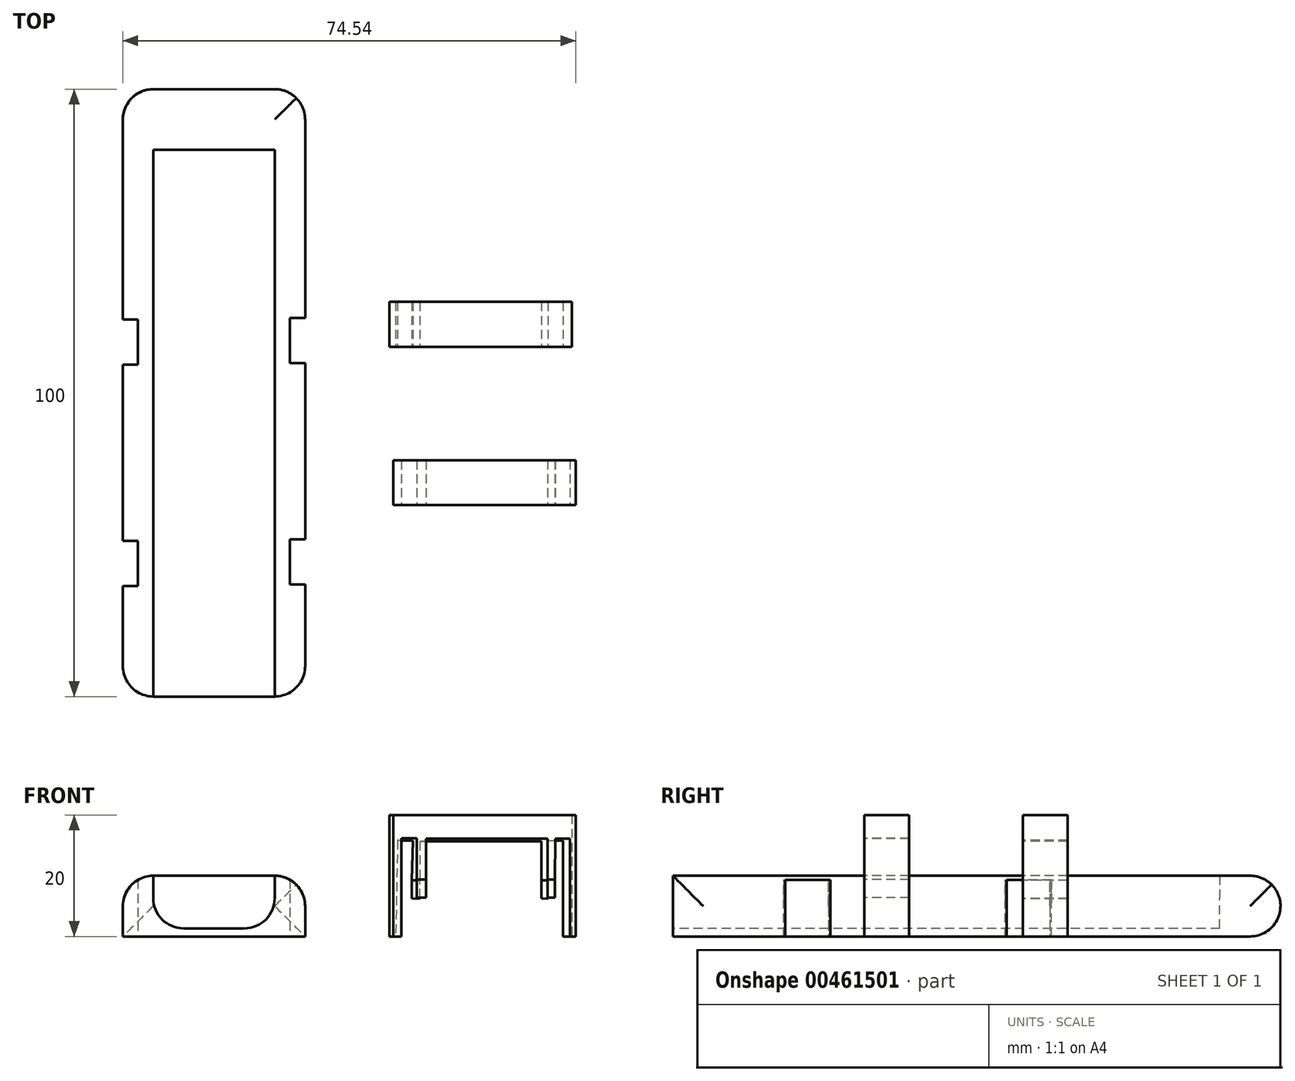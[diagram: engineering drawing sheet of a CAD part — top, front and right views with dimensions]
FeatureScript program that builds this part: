
annotation { "Feature Type Name" : "Feature", "Feature Type Description" : "" }
export const myFeature = defineFeature(function(context is Context, id is Id, definition is map)
    precondition{}
    {
        {
            var Q0;
            Q0=qCreatedBy(makeId("Top.planeOp"),FACE);
            var sketch = newSketch(context, id + "F0", { "sketchPlane" : qUnion([Q0])});
            skLineSegment(sketch, "E0.bottom", {"start": v(-21.76, -47.78) * mm, "end": v(8.24, -47.78) * mm});
            skLineSegment(sketch, "E0.top", {"start": v(-21.76, 52.22) * mm, "end": v(8.24, 52.22) * mm});
            skLineSegment(sketch, "E0.left", {"start": v(-21.76, -47.78) * mm, "end": v(-21.76, 52.22) * mm});
            skLineSegment(sketch, "E0.right", {"start": v(8.24, -47.78) * mm, "end": v(8.24, 52.22) * mm});
            skSolve(sketch);
        }
        {
            var Q0;
            Q0=makeQuery(id+"F0.imprint","IMPRINT",FACE,{"disambiguationData":[TD([[makeQuery(id+"F0.imprint","IMPRINT",EDGE,{"derivedFrom":sQuery(id+"F0.wireOp",EDGE,"E0.bottom")}),1.0]])]});
            extrude(context, id + "F1", {"entities" : qUnion([Q0]), "depth" : 10 * mm});
        }
        {
            var Q0;
            Q0=makeQuery(id+"F1.opExtrude","SWEPT_FACE",FACE,{"disambiguationData":[OSD([sQuery(id+"F0.wireOp",EDGE,"E0.bottom")])]});
            var sketch = newSketch(context, id + "F2", { "sketchPlane" : qUnion([Q0])});
            skLineSegment(sketch, "E1", {"start": v(-21.76, 10) * mm, "end": v(-16.76, 10) * mm});
            skLineSegment(sketch, "E2", {"start": v(-16.76, 10) * mm, "end": v(-16.76, 1.33) * mm});
            skLineSegment(sketch, "E3", {"start": v(-16.76, 1.33) * mm, "end": v(3.24, 1.33) * mm});
            skLineSegment(sketch, "E4", {"start": v(3.24, 1.33) * mm, "end": v(3.24, 10) * mm});
            skLineSegment(sketch, "E5", {"start": v(3.24, 10) * mm, "end": v(8.24, 10) * mm});
            skLineSegment(sketch, "E6", {"start": v(8.24, 10) * mm, "end": v(8.24, 0) * mm});
            skLineSegment(sketch, "E7", {"start": v(8.24, 0) * mm, "end": v(-21.76, 0) * mm});
            skLineSegment(sketch, "E8", {"start": v(-21.76, 0) * mm, "end": v(-21.76, 10) * mm});
            skSolve(sketch);
        }
        {
            var Q0;
            {var subQ0=sQuery(id+"F2.wireOp",EDGE,"E2");Q0=makeQuery(id+"F2.imprint","IMPRINT",FACE,{"disambiguationData":[TD([[makeQuery(id+"F2.imprint","IMPRINT",EDGE,{"derivedFrom":subQ0}),1.0]])]});}
            extrude(context, id + "F3", {"entities" : qUnion([Q0]), "operationType" : NewBodyOperationType.REMOVE, "oppositeDirection" : true, "depth" : 90 * mm});
        }
        {
            var Q0;
            Q0=makeQuery(id+"F3.boolean.opBoolean","COPY",EDGE,{"derivedFrom":makeQuery(id+"F3.opExtrude","CAP_EDGE",EDGE,{"disambiguationData":[OSD([sQuery(id+"F0.wireOp",EDGE,"E0.bottom")])],"isStart":false})});
            var Q1;
            Q1=makeQuery(id+"F1.opExtrude","CAP_EDGE",EDGE,{"disambiguationData":[OSD([sQuery(id+"F0.wireOp",EDGE,"E0.top")])],"isStart":false});
            var Q2;
            Q2=makeQuery(id+"F1.opExtrude","CAP_EDGE",EDGE,{"disambiguationData":[OSD([sQuery(id+"F0.wireOp",EDGE,"E0.top")])],"isStart":true});
            var Q3;
            Q3=makeQuery(id+"F1.opExtrude","SWEPT_EDGE",EDGE,{"disambiguationData":[OSD([sQuery(id+"F0.wireOp",EDGE,"E0.top"),sQuery(id+"F0.wireOp",EDGE,"E0.right")])]});
            var Q4;
            Q4=makeQuery(id+"F1.opExtrude","SWEPT_EDGE",EDGE,{"disambiguationData":[OSD([sQuery(id+"F0.wireOp",EDGE,"E0.top"),sQuery(id+"F0.wireOp",EDGE,"E0.left")])]});
            fillet(context, id + "F4", {"entities" : qUnion([Q0, Q1, Q2, Q3, Q4]), "radius" : 5 * mm, "tangentPropagation" : true, "allowEdgeOverflow" : false});
        }
        {
            var Q0;
            Q0=makeQuery(id+"F1.opExtrude","SWEPT_FACE",FACE,{"disambiguationData":[OSD([sQuery(id+"F0.wireOp",EDGE,"E0.right")])]});
            var sketch = newSketch(context, id + "F5", { "sketchPlane" : qUnion([Q0])});
            skLineSegment(sketch, "E9", {"start": v(-29.31, 10) * mm, "end": v(-29.31, 1.65) * mm});
            skLineSegment(sketch, "E10", {"start": v(-29.31, 1.65) * mm, "end": v(-21.88, 1.65) * mm});
            skLineSegment(sketch, "E11", {"start": v(-21.88, 1.65) * mm, "end": v(-21.88, 10) * mm});
            skLineSegment(sketch, "E12", {"start": v(-21.88, 10) * mm, "end": v(-29.31, 10) * mm});
            skLineSegment(sketch, "E13", {"start": v(7.15, 10) * mm, "end": v(7.15, 1.65) * mm});
            skLineSegment(sketch, "E14", {"start": v(7.15, 1.65) * mm, "end": v(14.55, 1.65) * mm});
            skLineSegment(sketch, "E15", {"start": v(14.55, 1.65) * mm, "end": v(14.55, 10) * mm});
            skLineSegment(sketch, "E16", {"start": v(14.55, 10) * mm, "end": v(7.15, 10) * mm});
            skLineSegment(sketch, "E17", {"start": v(14.55, 10) * mm, "end": v(14.55, 1.65) * mm});
            skLineSegment(sketch, "E18", {"start": v(7.15, 1.65) * mm, "end": v(7.15, 10) * mm});
            skSolve(sketch);
        }
        {
            var Q0;
            Q0=makeQuery(id+"F1.opExtrude","SWEPT_FACE",FACE,{"disambiguationData":[OSD([sQuery(id+"F0.wireOp",EDGE,"E0.left")])]});
            var sketch = newSketch(context, id + "F6", { "sketchPlane" : qUnion([Q0])});
            skLineSegment(sketch, "E19", {"start": v(-14.3, 10) * mm, "end": v(-14.3, 1.65) * mm});
            skLineSegment(sketch, "E20", {"start": v(-14.3, 1.65) * mm, "end": v(-6.9, 1.65) * mm});
            skLineSegment(sketch, "E21", {"start": v(-6.9, 1.65) * mm, "end": v(-6.9, 10) * mm});
            skLineSegment(sketch, "E22", {"start": v(-6.9, 10) * mm, "end": v(-14.3, 10) * mm});
            skLineSegment(sketch, "E23", {"start": v(22.17, 10) * mm, "end": v(22.17, 1.65) * mm});
            skLineSegment(sketch, "E24", {"start": v(22.17, 1.65) * mm, "end": v(29.57, 1.65) * mm});
            skLineSegment(sketch, "E25", {"start": v(29.57, 1.65) * mm, "end": v(29.57, 10) * mm});
            skLineSegment(sketch, "E26", {"start": v(29.57, 10) * mm, "end": v(22.17, 10) * mm});
            skSolve(sketch);
        }
        {
            var Q0;
            Q0=makeQuery(id+"F5.imprint","IMPRINT",FACE,{"disambiguationData":[TD([[makeQuery(id+"F5.imprint","IMPRINT",EDGE,{"derivedFrom":sQuery(id+"F5.wireOp",EDGE,"E9")}),1.0]])]});
            var Q1;
            Q1=makeQuery(id+"F5.imprint","IMPRINT",FACE,{"disambiguationData":[TD([[makeQuery(id+"F5.imprint","IMPRINT",EDGE,{"derivedFrom":sQuery(id+"F5.wireOp",EDGE,"E14")}),1.0]])]});
            extrude(context, id + "F7", {"entities" : qUnion([Q0, Q1]), "operationType" : NewBodyOperationType.REMOVE, "oppositeDirection" : true, "depth" : 2.5 * mm});
        }
        {
            var Q0;
            Q0=makeQuery(id+"F6.imprint","IMPRINT",FACE,{"disambiguationData":[TD([[makeQuery(id+"F6.imprint","IMPRINT",EDGE,{"derivedFrom":sQuery(id+"F6.wireOp",EDGE,"E19")}),1.0]])]});
            var Q1;
            Q1=makeQuery(id+"F6.imprint","IMPRINT",FACE,{"disambiguationData":[TD([[makeQuery(id+"F6.imprint","IMPRINT",EDGE,{"derivedFrom":sQuery(id+"F6.wireOp",EDGE,"E23")}),1.0]])]});
            extrude(context, id + "F8", {"entities" : qUnion([Q0, Q1]), "operationType" : NewBodyOperationType.REMOVE, "oppositeDirection" : true, "depth" : 2.5 * mm});
        }
        {
            var Q0;
            Q0=makeQuery(id+"F1.opExtrude","SWEPT_EDGE",EDGE,{"disambiguationData":[OSD([sQuery(id+"F0.wireOp",EDGE,"E0.bottom"),sQuery(id+"F0.wireOp",EDGE,"E0.left")])]});
            var Q1;
            Q1=makeQuery(id+"F1.opExtrude","SWEPT_EDGE",EDGE,{"disambiguationData":[OSD([sQuery(id+"F0.wireOp",EDGE,"E0.bottom"),sQuery(id+"F0.wireOp",EDGE,"E0.right")])]});
            fillet(context, id + "F9", {"entities" : qUnion([Q0, Q1]), "radius" : 5 * mm, "tangentPropagation" : true, "allowEdgeOverflow" : false});
        }
        {
            var Q0;
            {var subQ0=sQuery(id+"F0.wireOp",EDGE,"E0.right");Q0=makeQuery(id+"F7.boolean.opBoolean","SPLIT",EDGE,{"disambiguationData":[TD([makeQuery(id+"F7.opExtrude","SWEPT_FACE",FACE,{"disambiguationData":[OSD([sQuery(id+"F5.wireOp",EDGE,"E11")])]})])],"derivedFrom":makeQuery(id+"F1.opExtrude","CAP_EDGE",EDGE,{"disambiguationData":[OSD([subQ0])],"isStart":false})});}
            fillet(context, id + "F10", {"entities" : qUnion([Q0]), "radius" : 5 * mm, "tangentPropagation" : true, "allowEdgeOverflow" : false});
        }
        {
            var Q0;
            {var subQ0=sQuery(id+"F0.wireOp",EDGE,"E0.left");var subQ1=sQuery(id+"F0.wireOp",EDGE,"E0.top");Q0=makeQuery(id+"F8.boolean.opBoolean","SPLIT",EDGE,{"disambiguationData":[TD([makeQuery(id+"F4.opFillet","BLEND_FACE",FACE,{"disambiguationData":[OSD([subQ1])]})])],"derivedFrom":makeQuery(id+"F1.opExtrude","CAP_EDGE",EDGE,{"disambiguationData":[OSD([subQ0])],"isStart":false})});}
            fillet(context, id + "F11", {"entities" : qUnion([Q0]), "radius" : 5 * mm, "tangentPropagation" : true, "allowEdgeOverflow" : false});
        }
        {
            var Q0;
            Q0=makeQuery(id+"F3.boolean.opBoolean","COPY",EDGE,{"derivedFrom":makeQuery(id+"F3.opExtrude","SWEPT_EDGE",EDGE,{"disambiguationData":[OSD([sQuery(id+"F2.wireOp",EDGE,"E2"),sQuery(id+"F2.wireOp",EDGE,"E3")])]})});
            var Q1;
            Q1=makeQuery(id+"F3.boolean.opBoolean","COPY",EDGE,{"derivedFrom":makeQuery(id+"F3.opExtrude","SWEPT_EDGE",EDGE,{"disambiguationData":[OSD([sQuery(id+"F2.wireOp",EDGE,"E3"),sQuery(id+"F2.wireOp",EDGE,"E4")])]})});
            fillet(context, id + "F12", {"entities" : qUnion([Q0, Q1]), "radius" : 5 * mm, "tangentPropagation" : true, "allowEdgeOverflow" : false});
        }
        {
            var Q0;
            Q0=qCreatedBy(makeId("Top.planeOp"),FACE);
            var sketch = newSketch(context, id + "F13", { "sketchPlane" : qUnion([Q0])});
            skLineSegment(sketch, "E27.bottom", {"start": v(22.12, 17.2) * mm, "end": v(52.12, 17.2) * mm});
            skLineSegment(sketch, "E27.top", {"start": v(22.12, 9.8) * mm, "end": v(52.12, 9.8) * mm});
            skLineSegment(sketch, "E27.left", {"start": v(22.12, 17.2) * mm, "end": v(22.12, 9.8) * mm});
            skLineSegment(sketch, "E27.right", {"start": v(52.12, 17.2) * mm, "end": v(52.12, 9.8) * mm});
            skSolve(sketch);
        }
        {
            var Q0;
            Q0=makeQuery(id+"F13.imprint","IMPRINT",FACE,{"disambiguationData":[TD([[makeQuery(id+"F13.imprint","IMPRINT",EDGE,{"derivedFrom":sQuery(id+"F13.wireOp",EDGE,"E27.bottom")}),-1.0]])]});
            extrude(context, id + "F14", {"entities" : qUnion([Q0]), "depth" : 20 * mm});
        }
        {
            var Q0;
            Q0=makeQuery(id+"F14.opExtrude","SWEPT_FACE",FACE,{"disambiguationData":[OSD([sQuery(id+"F13.wireOp",EDGE,"E27.top")])]});
            var sketch = newSketch(context, id + "F15", { "sketchPlane" : qUnion([Q0])});
            skLineSegment(sketch, "E28", {"start": v(27.12, 0) * mm, "end": v(27.12, 15.65) * mm});
            skLineSegment(sketch, "E29", {"start": v(27.12, 15.65) * mm, "end": v(47.12, 15.65) * mm});
            skLineSegment(sketch, "E30", {"start": v(47.12, 15.65) * mm, "end": v(47.12, 0) * mm});
            skLineSegment(sketch, "E31", {"start": v(47.12, 0) * mm, "end": v(52.12, 0) * mm});
            skLineSegment(sketch, "E32", {"start": v(52.12, 0) * mm, "end": v(52.12, 20) * mm});
            skLineSegment(sketch, "E33", {"start": v(52.12, 20) * mm, "end": v(22.12, 20) * mm});
            skLineSegment(sketch, "E34", {"start": v(22.12, 20) * mm, "end": v(22.12, 0) * mm});
            skLineSegment(sketch, "E35", {"start": v(22.12, 0) * mm, "end": v(27.12, 0) * mm});
            skSolve(sketch);
        }
        {
            var Q0;
            {var subQ0=sQuery(id+"F15.wireOp",EDGE,"E28");Q0=makeQuery(id+"F15.imprint","IMPRINT",FACE,{"disambiguationData":[TD([[makeQuery(id+"F15.imprint","IMPRINT",EDGE,{"derivedFrom":subQ0}),-1.0]])]});}
            extrude(context, id + "F16", {"entities" : qUnion([Q0]), "operationType" : NewBodyOperationType.REMOVE, "oppositeDirection" : true, "depth" : 25 * mm});
        }
        {
            var Q0;
            Q0=makeQuery(id+"F14.opExtrude","SWEPT_FACE",FACE,{"disambiguationData":[OSD([sQuery(id+"F13.wireOp",EDGE,"E27.top")])]});
            var sketch = newSketch(context, id + "F17", { "sketchPlane" : qUnion([Q0])});
            skLineSegment(sketch, "E36", {"start": v(23.13, 0) * mm, "end": v(23.47, 15.83) * mm});
            skLineSegment(sketch, "E37", {"start": v(23.47, 15.83) * mm, "end": v(25.97, 15.77) * mm});
            skLineSegment(sketch, "E38", {"start": v(25.97, 15.77) * mm, "end": v(25.63, 0) * mm});
            skLineSegment(sketch, "E39", {"start": v(25.63, 0) * mm, "end": v(23.13, 0) * mm});
            skLineSegment(sketch, "E40", {"start": v(48.18, 0) * mm, "end": v(48.18, 15.78) * mm});
            skLineSegment(sketch, "E41", {"start": v(48.18, 15.78) * mm, "end": v(50.68, 15.78) * mm});
            skLineSegment(sketch, "E42", {"start": v(50.68, 15.78) * mm, "end": v(50.68, 0) * mm});
            skLineSegment(sketch, "E43", {"start": v(50.68, 0) * mm, "end": v(48.18, 0) * mm});
            skSolve(sketch);
        }
        {
            var Q0;
            Q0=makeQuery(id+"F17.imprint","IMPRINT",FACE,{"disambiguationData":[TD([[makeQuery(id+"F17.imprint","IMPRINT",EDGE,{"derivedFrom":sQuery(id+"F17.wireOp",EDGE,"E36")}),-1.0]])]});
            var Q1;
            Q1=makeQuery(id+"F17.imprint","IMPRINT",FACE,{"disambiguationData":[TD([[makeQuery(id+"F17.imprint","IMPRINT",EDGE,{"derivedFrom":sQuery(id+"F17.wireOp",EDGE,"E40")}),-1.0]])]});
            extrude(context, id + "F18", {"entities" : qUnion([Q0, Q1]), "operationType" : NewBodyOperationType.REMOVE, "oppositeDirection" : true, "depth" : 25 * mm});
        }
        {
            var Q0;
            Q0=makeQuery(id+"F7.boolean.opBoolean","COPY",FACE,{"derivedFrom":makeQuery(id+"F7.opExtrude","SWEPT_FACE",FACE,{"disambiguationData":[OSD([sQuery(id+"F5.wireOp",EDGE,"E10")])]})});
            var Q1;
            Q1=makeQuery(id+"F7.boolean.opBoolean","COPY",FACE,{"derivedFrom":makeQuery(id+"F7.opExtrude","SWEPT_FACE",FACE,{"disambiguationData":[OSD([sQuery(id+"F5.wireOp",EDGE,"E14")])]})});
            var Q2;
            Q2=makeQuery(id+"F8.boolean.opBoolean","COPY",FACE,{"derivedFrom":makeQuery(id+"F8.opExtrude","SWEPT_FACE",FACE,{"disambiguationData":[OSD([sQuery(id+"F6.wireOp",EDGE,"E24")])]})});
            var Q3;
            Q3=makeQuery(id+"F8.boolean.opBoolean","COPY",FACE,{"derivedFrom":makeQuery(id+"F8.opExtrude","SWEPT_FACE",FACE,{"disambiguationData":[OSD([sQuery(id+"F6.wireOp",EDGE,"E20")])]})});
            extrude(context, id + "F19", {"entities" : qUnion([Q0, Q1, Q2, Q3]), "operationType" : NewBodyOperationType.REMOVE, "oppositeDirection" : true, "depth" : 25 * mm});
        }
        {
            var Q0;
            Q0=qCreatedBy(makeId("Top.planeOp"),FACE);
            var sketch = newSketch(context, id + "F20", { "sketchPlane" : qUnion([Q0])});
            skLineSegment(sketch, "E44.bottom", {"start": v(22.78, -8.88) * mm, "end": v(52.78, -8.88) * mm});
            skLineSegment(sketch, "E44.top", {"start": v(22.78, -16.28) * mm, "end": v(52.78, -16.28) * mm});
            skLineSegment(sketch, "E44.left", {"start": v(22.78, -8.88) * mm, "end": v(22.78, -16.28) * mm});
            skLineSegment(sketch, "E44.right", {"start": v(52.78, -8.88) * mm, "end": v(52.78, -16.28) * mm});
            skSolve(sketch);
        }
        {
            var Q0;
            Q0=makeQuery(id+"F14.opExtrude","SWEPT_FACE",FACE,{"disambiguationData":[OSD([sQuery(id+"F13.wireOp",EDGE,"E27.top")])]});
            var sketch = newSketch(context, id + "F21", { "sketchPlane" : qUnion([Q0])});
            skLineSegment(sketch, "E45", {"start": v(25.83, 9.24) * mm, "end": v(27.12, 9.22) * mm});
            skLineSegment(sketch, "E46", {"start": v(27.12, 9.22) * mm, "end": v(27.12, 0) * mm});
            skLineSegment(sketch, "E47", {"start": v(27.12, 0) * mm, "end": v(25.63, 0) * mm});
            skLineSegment(sketch, "E48", {"start": v(25.63, 0) * mm, "end": v(25.83, 9.24) * mm});
            skLineSegment(sketch, "E49", {"start": v(47.12, 9.24) * mm, "end": v(48.18, 9.22) * mm});
            skLineSegment(sketch, "E50", {"start": v(48.18, 9.22) * mm, "end": v(48.18, 0) * mm});
            skLineSegment(sketch, "E51", {"start": v(48.18, 0) * mm, "end": v(47.12, 0) * mm});
            skLineSegment(sketch, "E52", {"start": v(47.12, 0) * mm, "end": v(47.12, 9.24) * mm});
            skSolve(sketch);
        }
        {
            var Q0;
            Q0=makeQuery(id+"F21.imprint","IMPRINT",FACE,{"disambiguationData":[TD([[makeQuery(id+"F21.imprint","IMPRINT",EDGE,{"derivedFrom":sQuery(id+"F21.wireOp",EDGE,"E45")}),-1.0]])]});
            var Q1;
            Q1=makeQuery(id+"F21.imprint","IMPRINT",FACE,{"disambiguationData":[TD([[makeQuery(id+"F21.imprint","IMPRINT",EDGE,{"derivedFrom":sQuery(id+"F21.wireOp",EDGE,"E49")}),-1.0]])]});
            extrude(context, id + "F22", {"entities" : qUnion([Q0, Q1]), "operationType" : NewBodyOperationType.REMOVE, "oppositeDirection" : true, "depth" : 25 * mm});
        }
        {
            var Q0;
            Q0=makeQuery(id+"F20.imprint","IMPRINT",FACE,{"disambiguationData":[TD([[makeQuery(id+"F20.imprint","IMPRINT",EDGE,{"derivedFrom":sQuery(id+"F20.wireOp",EDGE,"E44.bottom")}),-1.0]])]});
            extrude(context, id + "F23", {"entities" : qUnion([Q0]), "depth" : 20 * mm});
        }
        {
            var Q0;
            Q0=makeQuery(id+"F23.opExtrude","SWEPT_FACE",FACE,{"disambiguationData":[OSD([sQuery(id+"F20.wireOp",EDGE,"E44.top")])]});
            var sketch = newSketch(context, id + "F24", { "sketchPlane" : qUnion([Q0])});
            skLineSegment(sketch, "E53", {"start": v(28.15, 0) * mm, "end": v(28.15, 16.13) * mm});
            skLineSegment(sketch, "E54", {"start": v(28.15, 16.13) * mm, "end": v(48.15, 16.13) * mm});
            skLineSegment(sketch, "E55", {"start": v(48.15, 16.13) * mm, "end": v(48.15, 0) * mm});
            skLineSegment(sketch, "E56", {"start": v(48.15, 0) * mm, "end": v(28.15, 0) * mm});
            skSolve(sketch);
        }
        {
            var Q0;
            Q0=makeQuery(id+"F24.imprint","IMPRINT",FACE,{"disambiguationData":[TD([[makeQuery(id+"F24.imprint","IMPRINT",EDGE,{"derivedFrom":sQuery(id+"F24.wireOp",EDGE,"E53")}),-1.0]])]});
            extrude(context, id + "F25", {"entities" : qUnion([Q0]), "operationType" : NewBodyOperationType.REMOVE, "oppositeDirection" : true, "depth" : 25 * mm});
        }
        {
            var Q0;
            Q0=makeQuery(id+"F23.opExtrude","SWEPT_FACE",FACE,{"disambiguationData":[OSD([sQuery(id+"F20.wireOp",EDGE,"E44.top")])]});
            var sketch = newSketch(context, id + "F26", { "sketchPlane" : qUnion([Q0])});
            skLineSegment(sketch, "E57", {"start": v(24.1, 0) * mm, "end": v(24.1, 16.15) * mm});
            skLineSegment(sketch, "E58", {"start": v(24.1, 16.15) * mm, "end": v(26.6, 16.15) * mm});
            skLineSegment(sketch, "E59", {"start": v(26.6, 16.15) * mm, "end": v(26.6, 0) * mm});
            skLineSegment(sketch, "E60", {"start": v(26.6, 0) * mm, "end": v(24.1, 0) * mm});
            skLineSegment(sketch, "E61", {"start": v(49.42, 16.13) * mm, "end": v(51.81, 16.13) * mm});
            skLineSegment(sketch, "E62", {"start": v(51.81, 16.13) * mm, "end": v(51.81, 0) * mm});
            skLineSegment(sketch, "E63", {"start": v(51.81, 0) * mm, "end": v(49.31, 0) * mm});
            skLineSegment(sketch, "E64", {"start": v(49.31, 0) * mm, "end": v(49.42, 16.13) * mm});
            skSolve(sketch);
        }
        {
            var Q0;
            Q0=makeQuery(id+"F26.imprint","IMPRINT",FACE,{"disambiguationData":[TD([[makeQuery(id+"F26.imprint","IMPRINT",EDGE,{"derivedFrom":sQuery(id+"F26.wireOp",EDGE,"E57")}),-1.0]])]});
            var Q1;
            Q1=makeQuery(id+"F26.imprint","IMPRINT",FACE,{"disambiguationData":[TD([[makeQuery(id+"F26.imprint","IMPRINT",EDGE,{"derivedFrom":sQuery(id+"F26.wireOp",EDGE,"E61")}),-1.0]])]});
            extrude(context, id + "F27", {"entities" : qUnion([Q0, Q1]), "operationType" : NewBodyOperationType.REMOVE, "oppositeDirection" : true, "depth" : 25 * mm});
        }
        {
            var Q0;
            Q0=makeQuery(id+"F23.opExtrude","SWEPT_FACE",FACE,{"disambiguationData":[OSD([sQuery(id+"F20.wireOp",EDGE,"E44.top")])]});
            var sketch = newSketch(context, id + "F28", { "sketchPlane" : qUnion([Q0])});
            skLineSegment(sketch, "E65", {"start": v(26.6, 9.37) * mm, "end": v(28.15, 9.37) * mm});
            skPoint(sketch, "E65.endSnap0", {"position": v(28.15, 8.06) * mm});
            skLineSegment(sketch, "E66", {"start": v(28.15, 9.37) * mm, "end": v(28.15, 0) * mm});
            skLineSegment(sketch, "E67", {"start": v(28.15, 0) * mm, "end": v(26.6, 0) * mm});
            skLineSegment(sketch, "E68", {"start": v(26.6, 0) * mm, "end": v(26.6, 9.37) * mm});
            skLineSegment(sketch, "E69", {"start": v(48.15, 9.37) * mm, "end": v(49.37, 9.37) * mm});
            skLineSegment(sketch, "E70", {"start": v(49.37, 9.37) * mm, "end": v(49.31, 0) * mm});
            skLineSegment(sketch, "E71", {"start": v(49.31, 0) * mm, "end": v(48.15, 0) * mm});
            skLineSegment(sketch, "E72", {"start": v(48.15, 0) * mm, "end": v(48.15, 9.37) * mm});
            skSolve(sketch);
        }
        {
            var Q0;
            Q0=makeQuery(id+"F28.imprint","IMPRINT",FACE,{"disambiguationData":[TD([[makeQuery(id+"F28.imprint","IMPRINT",EDGE,{"derivedFrom":sQuery(id+"F28.wireOp",EDGE,"E65")}),-1.0]])]});
            var Q1;
            Q1=makeQuery(id+"F28.imprint","IMPRINT",FACE,{"disambiguationData":[TD([[makeQuery(id+"F28.imprint","IMPRINT",EDGE,{"derivedFrom":sQuery(id+"F28.wireOp",EDGE,"E69")}),-1.0]])]});
            extrude(context, id + "F29", {"entities" : qUnion([Q0, Q1]), "operationType" : NewBodyOperationType.REMOVE, "oppositeDirection" : true, "depth" : 25 * mm});
        }
        {
            var Q0;
            Q0=makeQuery(id+"F29.boolean.opBoolean","COPY",FACE,{"derivedFrom":makeQuery(id+"F29.opExtrude","SWEPT_FACE",FACE,{"disambiguationData":[OSD([sQuery(id+"F28.wireOp",EDGE,"E65")])]})});
            var Q1;
            Q1=makeQuery(id+"F29.boolean.opBoolean","COPY",FACE,{"derivedFrom":makeQuery(id+"F29.opExtrude","SWEPT_FACE",FACE,{"disambiguationData":[OSD([sQuery(id+"F28.wireOp",EDGE,"E69")])]})});
            var Q2;
            Q2=makeQuery(id+"F22.boolean.opBoolean","COPY",FACE,{"derivedFrom":makeQuery(id+"F22.opExtrude","SWEPT_FACE",FACE,{"disambiguationData":[OSD([sQuery(id+"F21.wireOp",EDGE,"E45")])]})});
            var Q3;
            Q3=makeQuery(id+"F22.boolean.opBoolean","COPY",FACE,{"derivedFrom":makeQuery(id+"F22.opExtrude","SWEPT_FACE",FACE,{"disambiguationData":[OSD([sQuery(id+"F21.wireOp",EDGE,"E49")])]})});
            extrude(context, id + "F30", {"entities" : qUnion([Q0, Q1, Q2, Q3]), "depth" : 3 * mm});
        }
    });
